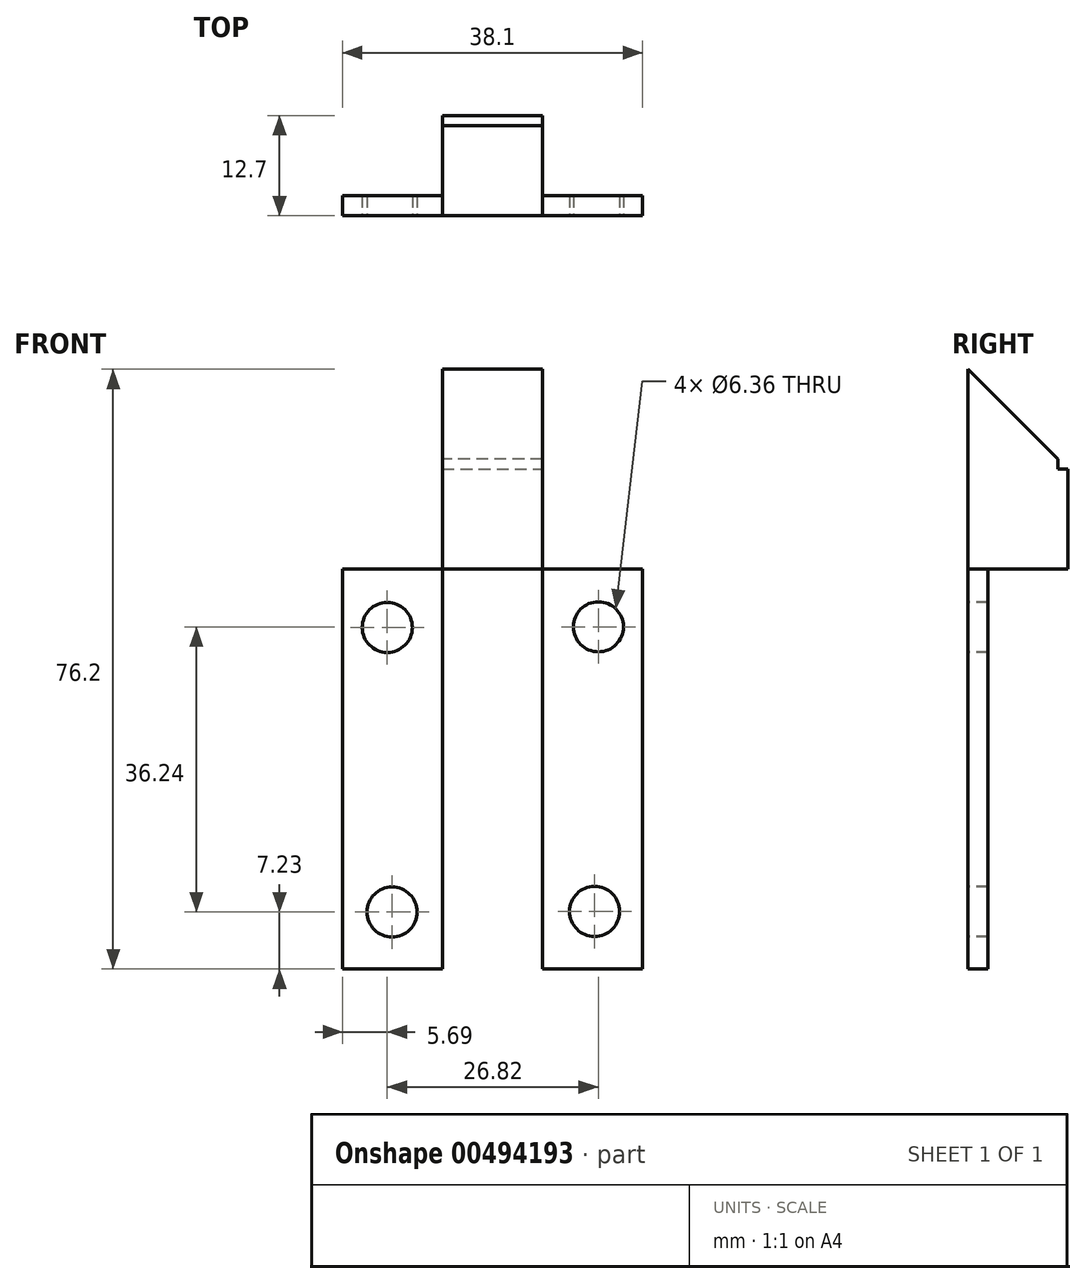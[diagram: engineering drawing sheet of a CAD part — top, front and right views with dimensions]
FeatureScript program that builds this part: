
annotation { "Feature Type Name" : "Feature", "Feature Type Description" : "" }
export const myFeature = defineFeature(function(context is Context, id is Id, definition is map)
    precondition{}
    {
        {
            var Q0;
            Q0=qCreatedBy(makeId("Front.planeOp"),FACE);
            var sketch = newSketch(context, id + "F0", { "sketchPlane" : qUnion([Q0])});
            skLineSegment(sketch, "E0.bottom", {"start": v(-26.1, 27.96) * mm, "end": v(12, 27.96) * mm});
            skLineSegment(sketch, "E0.top", {"start": v(-26.1, -22.84) * mm, "end": v(12, -22.84) * mm});
            skLineSegment(sketch, "E0.left", {"start": v(-26.1, 27.96) * mm, "end": v(-26.1, -22.84) * mm});
            skLineSegment(sketch, "E0.right", {"start": v(12, 27.96) * mm, "end": v(12, -22.84) * mm});
            skLineSegment(sketch, "E1.bottom", {"start": v(-13.4, -22.84) * mm, "end": v(-0.7, -22.84) * mm});
            skLineSegment(sketch, "E1.top", {"start": v(-13.4, 40.66) * mm, "end": v(-0.7, 40.66) * mm});
            skLineSegment(sketch, "E1.left", {"start": v(-13.4, -22.84) * mm, "end": v(-13.4, 40.66) * mm});
            skLineSegment(sketch, "E1.right", {"start": v(-0.7, -22.84) * mm, "end": v(-0.7, 40.66) * mm});
            skLineSegment(sketch, "E2.bottom", {"start": v(-13.4, 53.36) * mm, "end": v(-0.7, 53.36) * mm});
            skLineSegment(sketch, "E2.left", {"start": v(-13.4, 53.36) * mm, "end": v(-13.4, 40.66) * mm});
            skLineSegment(sketch, "E2.right", {"start": v(-0.7, 53.36) * mm, "end": v(-0.7, 40.66) * mm});
            skCircle(sketch, "E3", {"center": v(6.41, 20.63) * mm, "radius": 3.18 * mm});
            skCircle(sketch, "E4", {"center": v(5.93, -15.53) * mm, "radius": 3.18 * mm});
            skCircle(sketch, "E5", {"center": v(-20.41, 20.55) * mm, "radius": 3.18 * mm});
            skCircle(sketch, "E6", {"center": v(-19.8, -15.61) * mm, "radius": 3.18 * mm});
            skSolve(sketch);
        }
        {
            var Q0;
            {var subQ5=sQuery(id+"F0.wireOp",EDGE,"E1.bottom");Q0=makeQuery(id+"F0.imprint","IMPRINT",FACE,{"disambiguationData":[TD([[makeQuery(id+"F0.imprint","IMPRINT",EDGE,{"derivedFrom":subQ5}),1.0]])]});}
            var Q1;
            {var subQ5=sQuery(id+"F0.wireOp",EDGE,"E1.top");Q1=makeQuery(id+"F0.imprint","IMPRINT",FACE,{"disambiguationData":[TD([[makeQuery(id+"F0.imprint","IMPRINT",EDGE,{"derivedFrom":subQ5}),-1.0]])]});}
            extrude(context, id + "F1", {"entities" : qUnion([Q0, Q1]), "oppositeDirection" : true, "depth" : 12.7 * mm});
        }
        {
            var Q0;
            {var subQ5=sQuery(id+"F0.wireOp",EDGE,"E0.left");Q0=makeQuery(id+"F0.imprint","IMPRINT",FACE,{"disambiguationData":[TD([[makeQuery(id+"F0.imprint","IMPRINT",EDGE,{"derivedFrom":subQ5}),1.0]])]});}
            var Q1;
            {var subQ5=sQuery(id+"F0.wireOp",EDGE,"E0.right");Q1=makeQuery(id+"F0.imprint","IMPRINT",FACE,{"disambiguationData":[TD([[makeQuery(id+"F0.imprint","IMPRINT",EDGE,{"derivedFrom":subQ5}),-1.0]])]});}
            extrude(context, id + "F2", {"entities" : qUnion([Q0, Q1]), "oppositeDirection" : true, "depth" : 2.54 * mm});
        }
        {
            var Q0;
            Q0=makeQuery(id+"F0.imprint","IMPRINT",FACE,{"disambiguationData":[TD([[makeQuery(id+"F0.imprint","IMPRINT",EDGE,{"derivedFrom":sQuery(id+"F0.wireOp",EDGE,"E2.bottom")}),-1.0]])]});
            extrude(context, id + "F3", {"entities" : qUnion([Q0]), "operationType" : NewBodyOperationType.ADD, "oppositeDirection" : true, "depth" : 11.43 * mm});
        }
        {
            var Q0;
            Q0=makeQuery(id+"F3.boolean.opBoolean","MERGE",FACE,{"derivedFrom":[makeQuery(id+"F1.opExtrude","SWEPT_FACE",FACE,{"disambiguationData":[OSD([sQuery(id+"F0.wireOp",EDGE,"E1.left")])]}),makeQuery(id+"F3.opExtrude","SWEPT_FACE",FACE,{"disambiguationData":[OSD([sQuery(id+"F0.wireOp",EDGE,"E2.left")])]})]});
            var sketch = newSketch(context, id + "F4", { "sketchPlane" : qUnion([Q0])});
            skLineSegment(sketch, "E7.bottom", {"start": v(-11.43, 53.36) * mm, "end": v(0, 53.36) * mm});
            skLineSegment(sketch, "E7.top", {"start": v(-11.43, 41.93) * mm, "end": v(0, 41.93) * mm});
            skLineSegment(sketch, "E7.left", {"start": v(-11.43, 53.36) * mm, "end": v(-11.43, 41.93) * mm});
            skLineSegment(sketch, "E7.right", {"start": v(0, 53.36) * mm, "end": v(0, 41.93) * mm});
            skLineSegment(sketch, "E8", {"start": v(0, 53.36) * mm, "end": v(-11.43, 41.93) * mm});
            skSolve(sketch);
        }
        {
            var Q0;
            Q0=makeQuery(id+"F4.imprint","IMPRINT",FACE,{"disambiguationData":[TD([[makeQuery(id+"F4.imprint","IMPRINT",EDGE,{"derivedFrom":sQuery(id+"F4.wireOp",EDGE,"E7.bottom")}),-1.0]])]});
            extrude(context, id + "F5", {"entities" : qUnion([Q0]), "operationType" : NewBodyOperationType.REMOVE, "oppositeDirection" : true, "depth" : 12.7 * mm});
        }
    });
